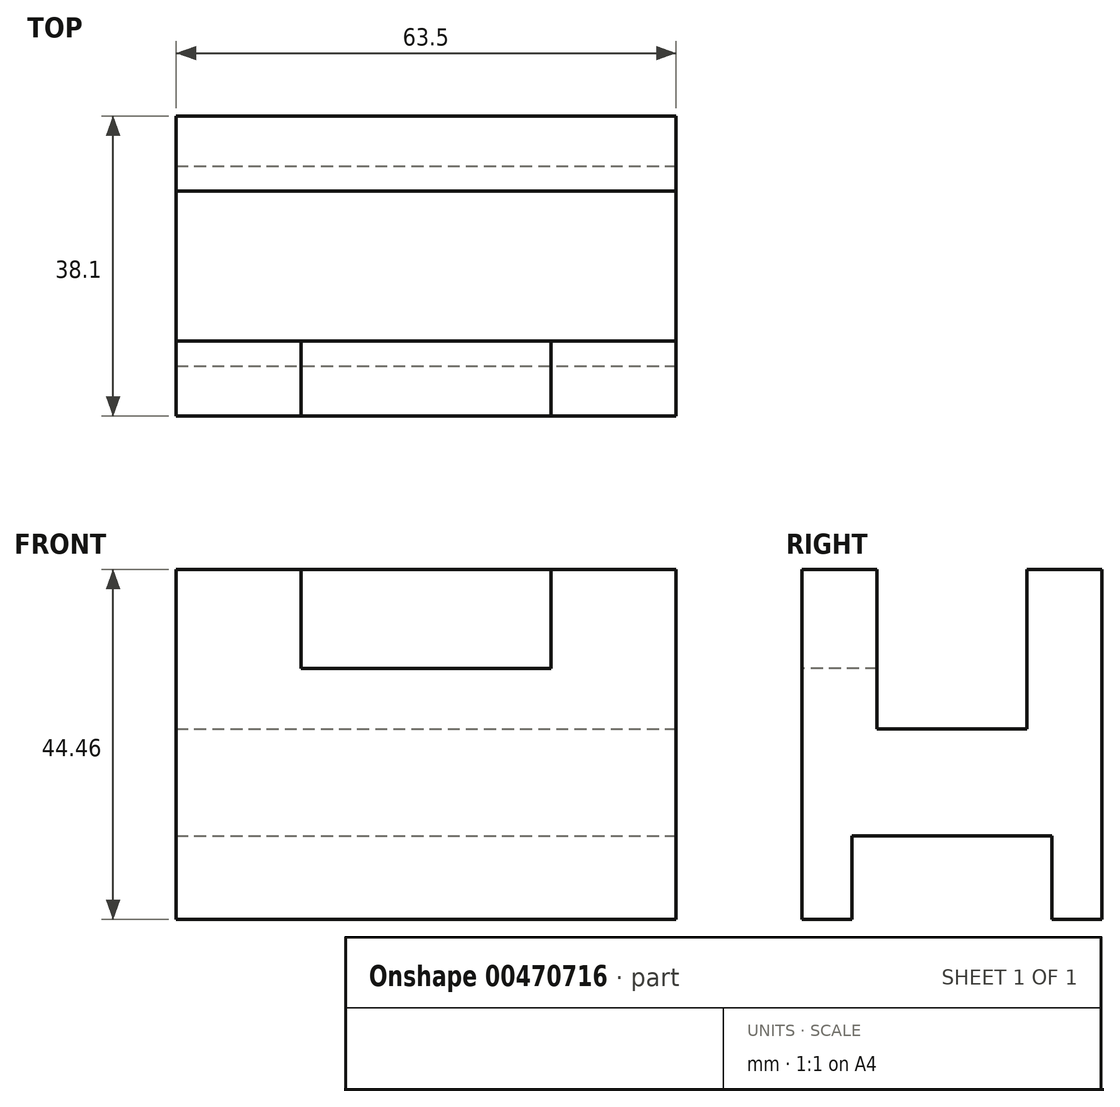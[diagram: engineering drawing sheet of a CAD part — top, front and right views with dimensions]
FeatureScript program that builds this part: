
annotation { "Feature Type Name" : "Feature", "Feature Type Description" : "" }
export const myFeature = defineFeature(function(context is Context, id is Id, definition is map)
    precondition{}
    {
        {
            var Q0;
            Q0=qCreatedBy(makeId("Front.planeOp"),FACE);
            var sketch = newSketch(context, id + "F0", { "sketchPlane" : qUnion([Q0])});
            skLineSegment(sketch, "E0.bottom", {"start": v(31.75, 22.23) * mm, "end": v(-31.75, 22.23) * mm});
            skLineSegment(sketch, "E0.top", {"start": v(31.75, -22.23) * mm, "end": v(-31.75, -22.23) * mm});
            skLineSegment(sketch, "E0.left", {"start": v(31.75, 22.23) * mm, "end": v(31.75, -22.23) * mm});
            skLineSegment(sketch, "E0.right", {"start": v(-31.75, 22.23) * mm, "end": v(-31.75, -22.23) * mm});
            skPoint(sketch, "E0.middle", {"position": v(0, 0) * mm});
            skSolve(sketch);
        }
        {
            var Q0;
            Q0=makeQuery(id+"F0.imprint","IMPRINT",FACE,{"disambiguationData":[TD([[makeQuery(id+"F0.imprint","IMPRINT",EDGE,{"derivedFrom":sQuery(id+"F0.wireOp",EDGE,"E0.bottom")}),1.0]])]});
            extrude(context, id + "F1", {"entities" : qUnion([Q0]), "depth" : 38.1 * mm});
        }
        {
            var Q0;
            Q0=makeQuery(id+"F1.opExtrude","CAP_FACE",FACE,{"disambiguationData":[OSD([sQuery(id+"F0.wireOp",EDGE,"E0.bottom"),sQuery(id+"F0.wireOp",EDGE,"E0.top"),sQuery(id+"F0.wireOp",EDGE,"E0.left"),sQuery(id+"F0.wireOp",EDGE,"E0.right")])],"isStart":false});
            var sketch = newSketch(context, id + "F2", { "sketchPlane" : qUnion([Q0])});
            skLineSegment(sketch, "E1.bottom", {"start": v(-15.88, 22.23) * mm, "end": v(15.88, 22.23) * mm});
            skLineSegment(sketch, "E1.top", {"start": v(-15.88, 9.69) * mm, "end": v(15.88, 9.69) * mm});
            skLineSegment(sketch, "E1.left", {"start": v(-15.88, 22.23) * mm, "end": v(-15.88, 9.69) * mm});
            skLineSegment(sketch, "E1.right", {"start": v(15.88, 22.23) * mm, "end": v(15.88, 9.69) * mm});
            skSolve(sketch);
        }
        {
            var Q0;
            Q0=makeQuery(id+"F1.opExtrude","SWEPT_FACE",FACE,{"disambiguationData":[OSD([sQuery(id+"F0.wireOp",EDGE,"E0.left")])]});
            var sketch = newSketch(context, id + "F3", { "sketchPlane" : qUnion([Q0])});
            skLineSegment(sketch, "E2.bottom", {"start": v(-28.57, 22.23) * mm, "end": v(-9.53, 22.23) * mm});
            skLineSegment(sketch, "E2.top", {"start": v(-28.57, 1.98) * mm, "end": v(-9.53, 1.98) * mm});
            skLineSegment(sketch, "E2.left", {"start": v(-28.57, 22.23) * mm, "end": v(-28.57, 1.98) * mm});
            skLineSegment(sketch, "E2.right", {"start": v(-9.53, 22.23) * mm, "end": v(-9.53, 1.98) * mm});
            skSolve(sketch);
        }
        {
            var Q0;
            Q0=makeQuery(id+"F3.imprint","IMPRINT",FACE,{"disambiguationData":[TD([[makeQuery(id+"F3.imprint","IMPRINT",EDGE,{"derivedFrom":sQuery(id+"F3.wireOp",EDGE,"E2.bottom")}),-1.0]])]});
            extrude(context, id + "F4", {"entities" : qUnion([Q0]), "operationType" : NewBodyOperationType.REMOVE, "oppositeDirection" : true, "depth" : 63.5 * mm});
        }
        {
            var Q0;
            Q0=makeQuery(id+"F2.imprint","IMPRINT",FACE,{"disambiguationData":[TD([[makeQuery(id+"F2.imprint","IMPRINT",EDGE,{"derivedFrom":sQuery(id+"F2.wireOp",EDGE,"E1.bottom")}),1.0]])]});
            extrude(context, id + "F5", {"entities" : qUnion([Q0]), "operationType" : NewBodyOperationType.REMOVE, "oppositeDirection" : true, "depth" : 25.4 * mm});
        }
        {
            var Q0;
            Q0=makeQuery(id+"F1.opExtrude","SWEPT_FACE",FACE,{"disambiguationData":[OSD([sQuery(id+"F0.wireOp",EDGE,"E0.left")])]});
            var sketch = newSketch(context, id + "F6", { "sketchPlane" : qUnion([Q0])});
            skLineSegment(sketch, "E3.bottom", {"start": v(-31.75, -22.23) * mm, "end": v(-6.35, -22.23) * mm});
            skLineSegment(sketch, "E3.top", {"start": v(-31.75, -11.63) * mm, "end": v(-6.35, -11.63) * mm});
            skLineSegment(sketch, "E3.left", {"start": v(-31.75, -22.23) * mm, "end": v(-31.75, -11.63) * mm});
            skLineSegment(sketch, "E3.right", {"start": v(-6.35, -22.23) * mm, "end": v(-6.35, -11.63) * mm});
            skSolve(sketch);
        }
        {
            var Q0;
            Q0=makeQuery(id+"F6.imprint","IMPRINT",FACE,{"disambiguationData":[TD([[makeQuery(id+"F6.imprint","IMPRINT",EDGE,{"derivedFrom":sQuery(id+"F6.wireOp",EDGE,"E3.bottom")}),1.0]])]});
            extrude(context, id + "F7", {"entities" : qUnion([Q0]), "operationType" : NewBodyOperationType.REMOVE, "oppositeDirection" : true, "depth" : 63.5 * mm});
        }
    });
